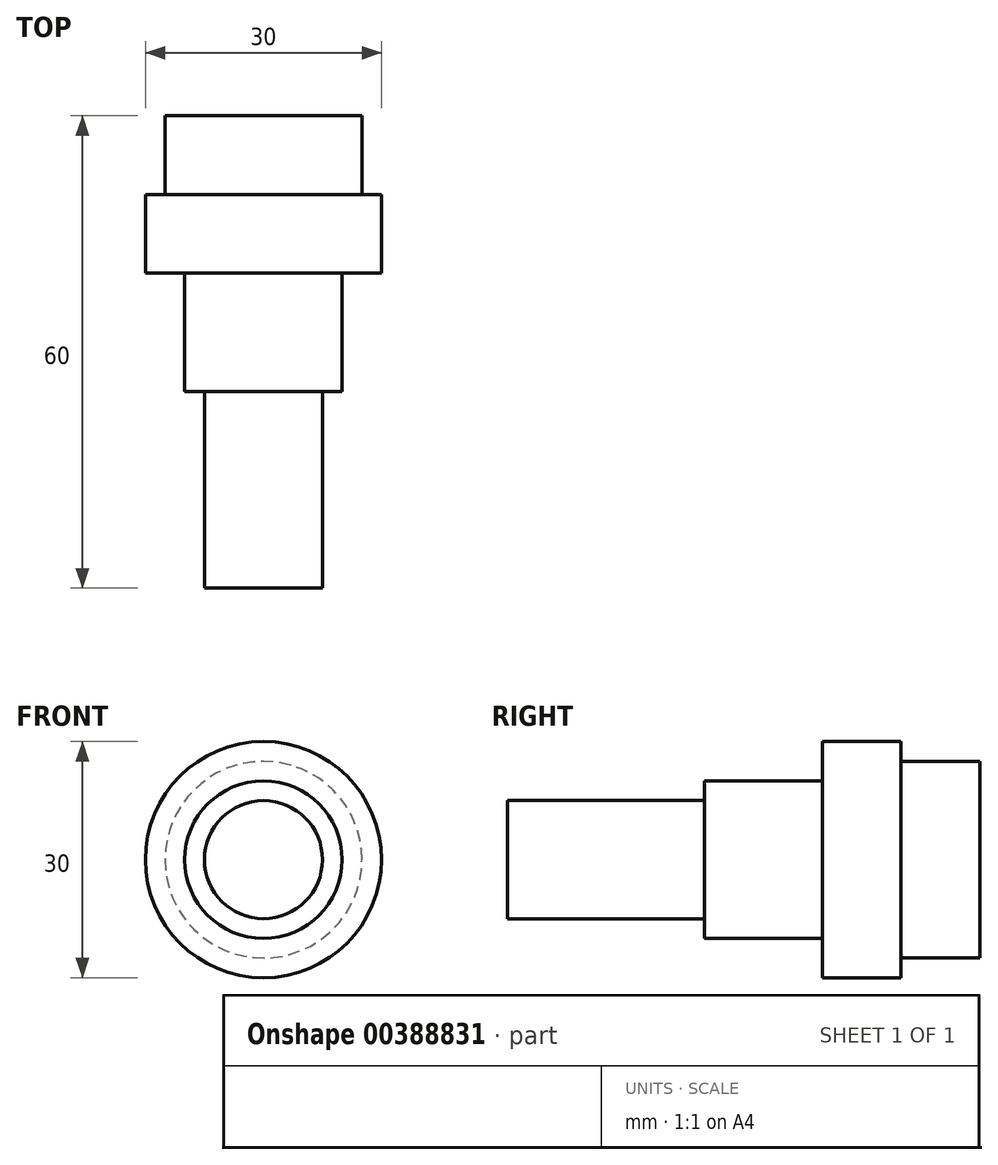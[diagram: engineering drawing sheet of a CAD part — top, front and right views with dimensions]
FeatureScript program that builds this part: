
annotation { "Feature Type Name" : "Feature", "Feature Type Description" : "" }
export const myFeature = defineFeature(function(context is Context, id is Id, definition is map)
    precondition{}
    {
        {
            var Q0;
            Q0=qCreatedBy(makeId("Front.planeOp"),FACE);
            var sketch = newSketch(context, id + "F0", { "sketchPlane" : qUnion([Q0])});
            skCircle(sketch, "E0", {"center": v(0, 0) * mm, "radius": 7.5 * mm});
            skSolve(sketch);
        }
        {
            var Q0;
            Q0 = qSketchRegion(id + "F0", true);
            extrude(context, id + "F1", {"entities" : qUnion([Q0]), "depth" : 25 * mm});
        }
        {
            var Q0;
            Q0=makeQuery(id+"F1.opExtrude","CAP_FACE",FACE,{"disambiguationData":[OSD([sQuery(id+"F0.wireOp",EDGE,"E0")])],"isStart":true});
            var sketch = newSketch(context, id + "F2", { "sketchPlane" : qUnion([Q0])});
            skCircle(sketch, "E1", {"center": v(0, 0) * mm, "radius": 10 * mm});
            skSolve(sketch);
        }
        {
            var Q0;
            Q0 = qSketchRegion(id + "F2", true);
            extrude(context, id + "F3", {"entities" : qUnion([Q0]), "operationType" : NewBodyOperationType.ADD, "depth" : 15 * mm});
        }
        {
            var Q0;
            Q0=makeQuery(id+"F3.opExtrude","CAP_FACE",FACE,{"disambiguationData":[OSD([sQuery(id+"F2.wireOp",EDGE,"E1")])],"isStart":false});
            var sketch = newSketch(context, id + "F4", { "sketchPlane" : qUnion([Q0])});
            skCircle(sketch, "E2", {"center": v(0, 0) * mm, "radius": 15 * mm});
            skSolve(sketch);
        }
        {
            var Q0;
            Q0 = qSketchRegion(id + "F4", true);
            extrude(context, id + "F5", {"entities" : qUnion([Q0]), "operationType" : NewBodyOperationType.ADD, "depth" : 10 * mm});
        }
        {
            var Q0;
            Q0=makeQuery(id+"F5.opExtrude","CAP_FACE",FACE,{"disambiguationData":[OSD([sQuery(id+"F4.wireOp",EDGE,"E2")])],"isStart":false});
            var sketch = newSketch(context, id + "F6", { "sketchPlane" : qUnion([Q0])});
            skCircle(sketch, "E3", {"center": v(0, 0) * mm, "radius": 12.5 * mm});
            skSolve(sketch);
        }
        {
            var Q0;
            Q0 = qSketchRegion(id + "F6", true);
            extrude(context, id + "F7", {"entities" : qUnion([Q0]), "operationType" : NewBodyOperationType.ADD, "depth" : 10 * mm});
        }
    });
